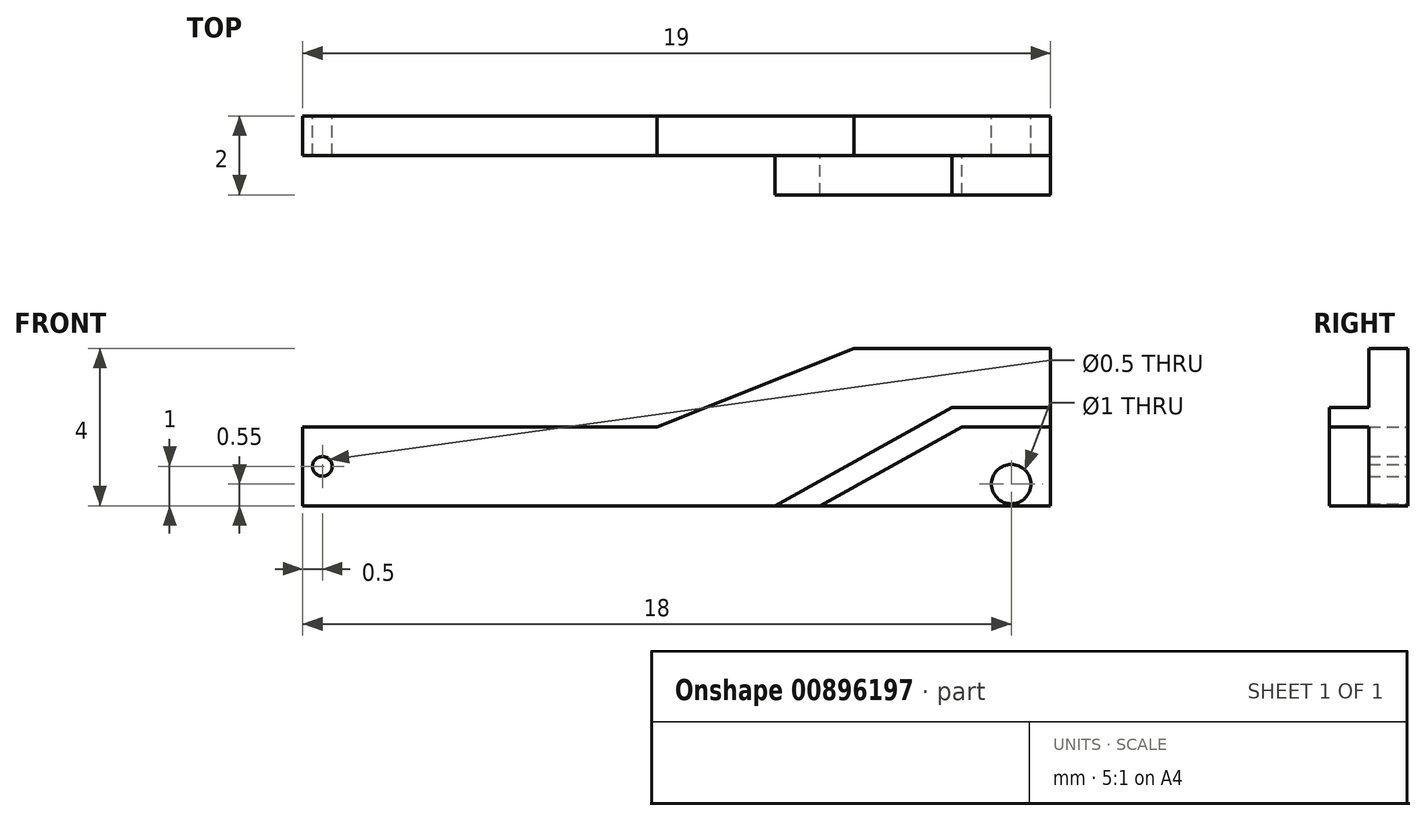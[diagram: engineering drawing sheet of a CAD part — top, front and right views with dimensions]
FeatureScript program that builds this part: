
annotation { "Feature Type Name" : "Feature", "Feature Type Description" : "" }
export const myFeature = defineFeature(function(context is Context, id is Id, definition is map)
    precondition{}
    {
        {
            var Q0;
            Q0=qCreatedBy(makeId("Front.planeOp"),FACE);
            var sketch = newSketch(context, id + "F0", { "sketchPlane" : qUnion([Q0])});
            skLineSegment(sketch, "E0", {"start": v(7, 4) * mm, "end": v(7, 0) * mm});
            skLineSegment(sketch, "E1", {"start": v(0, 0) * mm, "end": v(7, 0) * mm});
            skPoint(sketch, "E2.orphan", {"position": v(7, 0) * mm});
            skLineSegment(sketch, "E3", {"start": v(0, 0) * mm, "end": v(-11, 0) * mm});
            skLineSegment(sketch, "E4", {"start": v(-11, 2) * mm, "end": v(-3, 2) * mm});
            skLineSegment(sketch, "E5", {"start": v(7, 4) * mm, "end": v(4, 4) * mm});
            skLineSegment(sketch, "E6.0", {"start": v(-12, 2) * mm, "end": v(-12, 0) * mm});
            skLineSegment(sketch, "E7", {"start": v(-11, 2) * mm, "end": v(-12, 2) * mm});
            skLineSegment(sketch, "E8", {"start": v(-11, 0) * mm, "end": v(-12, 0) * mm});
            skCircle(sketch, "E9", {"center": v(-11.5, 1) * mm, "radius": 0.25 * mm});
            skCircle(sketch, "E10", {"center": v(6, 0.55) * mm, "radius": 0.5 * mm});
            skLineSegment(sketch, "E11", {"start": v(4, 4) * mm, "end": v(2, 4) * mm});
            skLineSegment(sketch, "E12", {"start": v(2, 4) * mm, "end": v(-3, 2) * mm});
            skSolve(sketch);
        }
        {
            var Q0;
            Q0 = qSketchRegion(id + "F0", true);
            extrude(context, id + "F1", {"entities" : qUnion([Q0]), "depth" : 1 * mm, "offsetDistance" : 25 * mm});
        }
        {
            var Q0;
            Q0=makeQuery(id+"F1.opExtrude","CAP_FACE",FACE,{"disambiguationData":[OSD([sQuery(id+"F0.wireOp",EDGE,"E0"),sQuery(id+"F0.wireOp",EDGE,"E1"),sQuery(id+"F0.wireOp",EDGE,"E3"),sQuery(id+"F0.wireOp",EDGE,"E4"),sQuery(id+"F0.wireOp",EDGE,"E5"),sQuery(id+"F0.wireOp",EDGE,"824dd725-580e-4600-9717-29947750375b"),sQuery(id+"F0.wireOp",EDGE,"E6.0"),sQuery(id+"F0.wireOp",EDGE,"E7"),sQuery(id+"F0.wireOp",EDGE,"E8"),sQuery(id+"F0.wireOp",EDGE,"E9")])],"isStart":false});
            var sketch = newSketch(context, id + "F2", { "sketchPlane" : qUnion([Q0])});
            skLineSegment(sketch, "E13", {"start": v(0, 0) * mm, "end": v(4.5, 2.5) * mm});
            skLineSegment(sketch, "E14", {"start": v(4.5, 2.5) * mm, "end": v(7, 2.5) * mm});
            skLineSegment(sketch, "E15", {"start": v(7, 2.5) * mm, "end": v(7, 2) * mm});
            skLineSegment(sketch, "E16", {"start": v(7, 2) * mm, "end": v(4.75, 2) * mm});
            skLineSegment(sketch, "E17", {"start": v(4.75, 2) * mm, "end": v(1.15, 0) * mm});
            skLineSegment(sketch, "E18", {"start": v(1.15, 0) * mm, "end": v(0, 0) * mm});
            skSolve(sketch);
        }
        {
            var Q0;
            Q0 = qSketchRegion(id + "F2", true);
            extrude(context, id + "F3", {"entities" : qUnion([Q0]), "operationType" : NewBodyOperationType.ADD, "depth" : 1 * mm, "offsetDistance" : 25 * mm});
        }
    });
